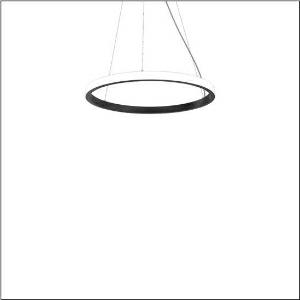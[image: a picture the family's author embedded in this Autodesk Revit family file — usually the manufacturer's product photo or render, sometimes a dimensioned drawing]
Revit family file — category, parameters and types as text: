
# Revit family: silica_r__21_ring-o_5pjbo2d3104a_e544
name_source: partatom
category: Lighting Fixtures
units: mm (PartAtom-declared; Revit-internal decimal feet)

## family parameters
Cut with Voids When Loaded = No
Host = Face
Light Source = No
Part Type = Normal
Room Calculation Point = No
Round Connector Dimension = Use Diameter
Shared = No

## types (1)
- Silica® 21 Ring-O (1 x LED, 4940 lm, 80 W, 4000K)
    Apparent Load = 80 VA
    CIE Flux Codes = 2 16 49 50 100
    Color Rendering = 80
    Color Temperature = 4000K
    Default Elevation = 1800 mm
    Description = Silica® 21 Ring-O, suspended luminaire, of PMMA, frosted, light emission: outer ring side luminous distribution, primary light characteristic: symmetric, installation type: suspended mounting, LED, rated luminous flux: 4.940lm, luminous efficacy: 62lm/W, light colour: 840, colour temperature: 4000K, control gear: DALI 2, with terminal, 5-pole, mains connection: 230V, AC/DC, 0/50..60Hz, rated input power: 80W, housing, of extruded aluminium section, jet black (RAL 9005), diameter: 810mm, ceiling canopy, jet black (RAL 9005), protection rating (lamp compartment): IP40, insulation class (complete): insulation class I (protective earthing), certification: CE, impact resistance: IK02, permissible operating ambient temperature: 0..+35°C, packaging unit: 1 piece
    Height = 48 mm  [stored 0.15748 ft]
    Lamp = 1 x LED
    Lamp Light Flux = 4940 lm
    Lamp Power = 80 W
    Lamp count = 1
    Length = 810 mm
    Luminous efficacy = 62 lm/W
    Manufacturer = Siteco
    ModVariant = No
    Model = 5PJBO2D3104A
    Mounting Place = Ceiling
    Mounting Type = Pendant
    Number of Poles = 1
    OnlyDefault = Yes
    Power Factor = 1
    Product Name = Silica® 21 Ring-O
    Product group = suspended luminaire
    ProductGroupID = 905
    Protection Class = Protection class I
    Protection Degree = IP 40
    RLX_Detail_Level = 1
    RLX_Emergency_Light_Flux = 0 lm
    RLX_Emergency_Type = 0
    RLX_Emergency_Type_DB = No
    RlxData = <blob elided: 14089 chars, md5=9ea38214>
    Socket = socket
    Standby Power = 0 W
    System Light Flux = 4940 lm
    System Power = 80 W
    Type Comments = Product without accessories
    Type Image = l_1258381.jpg
    URL = http://relux.com
    VarID = ---
    Voltage = 0 V
    Weight = 0.00 kg
    Width = 0 mm  [stored 0 ft]

note: [stored X ft] marks values corroborated as IEEE doubles in the binary element streams (Revit-internal decimal feet)

## geometry (parser evidence)
native form markers: Sweep x13
no freeform markers — native parametric forms only
